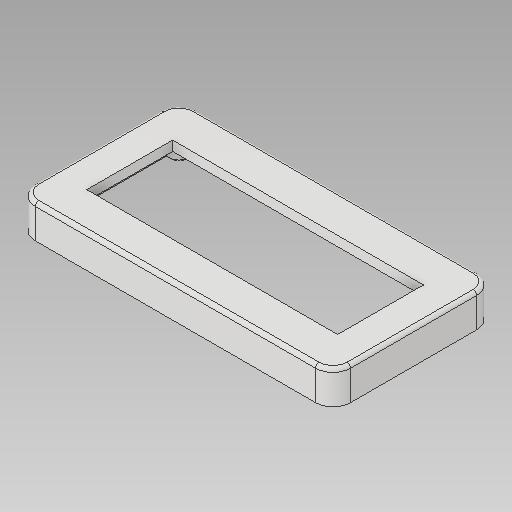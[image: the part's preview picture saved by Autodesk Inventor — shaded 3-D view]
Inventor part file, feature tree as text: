
AUTODESK INVENTOR PART (.ipt)
format: ipt  version: 2019 (Build 230136000, 136)  size: 428,032 bytes
history: native  units: mm
features: projected_geometry x5, sketch x4, extrude x3, fillet x3, other x1, shell x1, hole x1
ambient origin geometry x8: Origin, YZ Plane, XZ Plane, XY Plane, X Axis, Y Axis, Z Axis, Center Point
bodies: Body1 (feature_tree)
feature tree (18):
  other  "Sólido1"
  extrude  "Extrusión1"  Depth=46.0mm
  fillet  "Empalme1"  Radius=9.5mm
  shell  "Vaciado1"  Thickness=5.0mm
  fillet  "Empalme2"  Radius=2.8mm
  extrude  "Extrusión2"  Depth=11.0mm
  extrude  "Extrusión3"  Depth=71.6mm
  fillet  "Empalme3"  Radius=9.5mm
  hole  "Agujero1"  [1 undecoded]
  sketch  "Boceto1"  dims[d0=90.0mm d1=46.0mm d2=9.5mm d3=0.0mm d4=5.0mm d5=2.8mm]
  sketch  "Boceto2"  dims[d6=1.0mm d7=11.0mm]
  sketch  "Boceto3"  dims[d10=24.5mm d11=71.6mm d12=9.5mm d13=0.0mm]
  projected_geometry  "Contorno proyectado1"
  sketch  "Boceto4"  dims[d14=23.0mm d15=75.0mm d16=31.0mm d17=5.5mm d18=5.5mm d19=5.5mm d20=5.5mm d21=3.3mm d22=0.0mm d23=0.5mm d24=1.8mm d25=6.0mm d26=2.5mm d27=2.0mm d28=90.0deg d29=4.0mm d30=20.594885mm]
  projected_geometry  "Contorno proyectado2"
  projected_geometry  "Contorno proyectado3"
  projected_geometry  "Contorno proyectado4"
  projected_geometry  "Contorno proyectado5"
note: 1 required parameter value undecoded (feature->parameter linkage not recoverable at this tier; creation-order binding heuristic only, values carry confidence <= 0.55)
